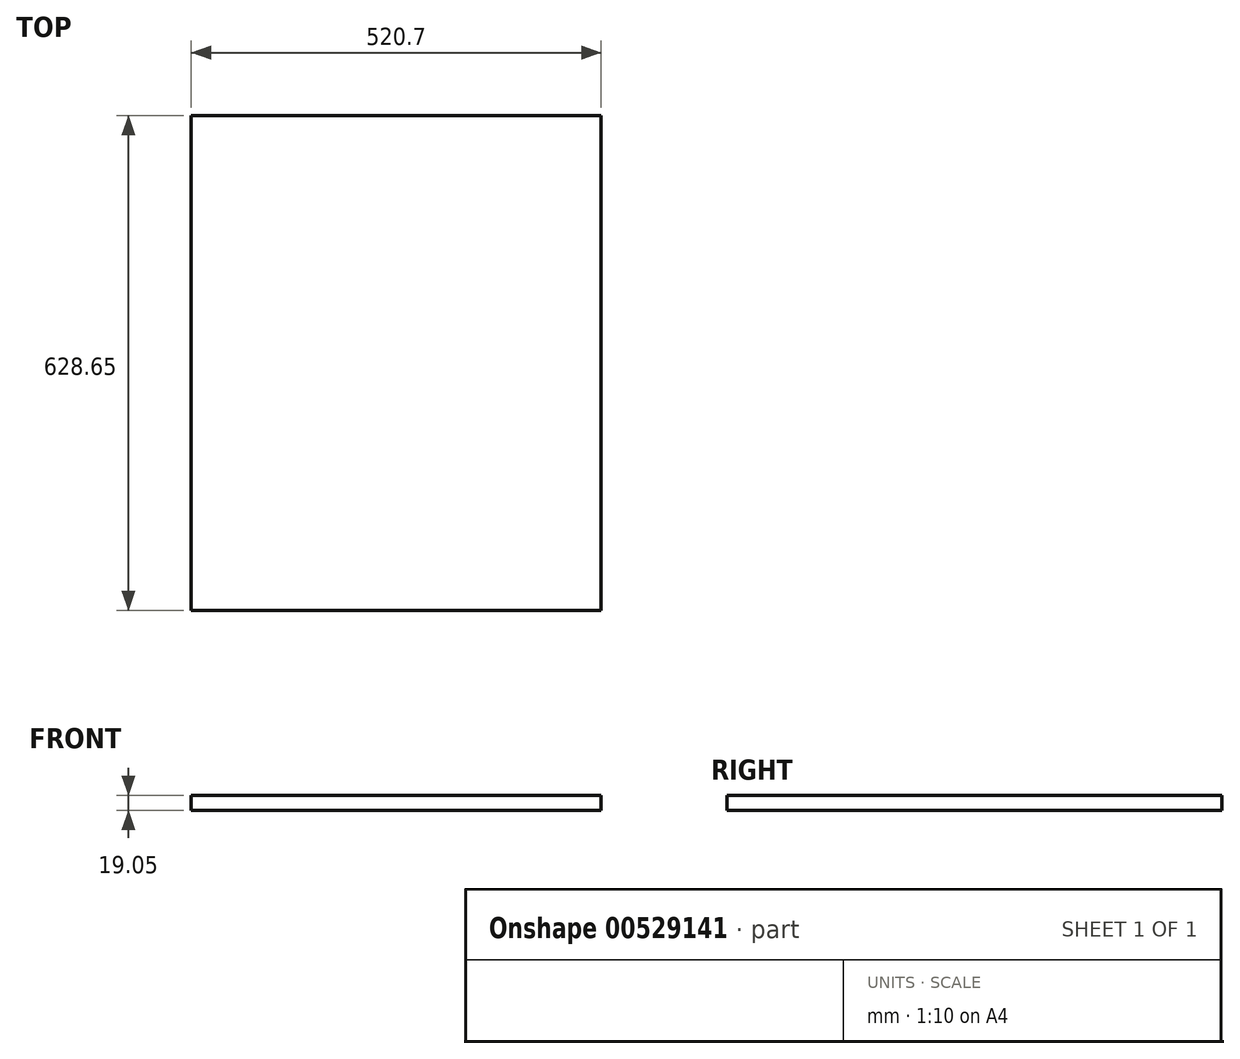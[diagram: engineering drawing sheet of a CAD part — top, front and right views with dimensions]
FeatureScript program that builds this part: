
annotation { "Feature Type Name" : "Feature", "Feature Type Description" : "" }
export const myFeature = defineFeature(function(context is Context, id is Id, definition is map)
    precondition{}
    {
        {
            var Q0;
            Q0=qCreatedBy(makeId("Top.planeOp"),FACE);
            var sketch = newSketch(context, id + "F0", { "sketchPlane" : qUnion([Q0])});
            skLineSegment(sketch, "E0.bottom", {"start": v(207.26, 0) * mm, "end": v(-313.44, 0) * mm});
            skLineSegment(sketch, "E0.top", {"start": v(207.26, -628.65) * mm, "end": v(-313.44, -628.65) * mm});
            skLineSegment(sketch, "E0.left", {"start": v(207.26, 0) * mm, "end": v(207.26, -628.65) * mm});
            skLineSegment(sketch, "E0.right", {"start": v(-313.44, 0) * mm, "end": v(-313.44, -628.65) * mm});
            skSolve(sketch);
        }
        {
            var Q0;
            Q0 = qSketchRegion(id + "F0", true);
            extrude(context, id + "F1", {"entities" : qUnion([Q0]), "depth" : 19.05 * mm, "offsetDistance" : 25.4 * mm});
        }
    });
